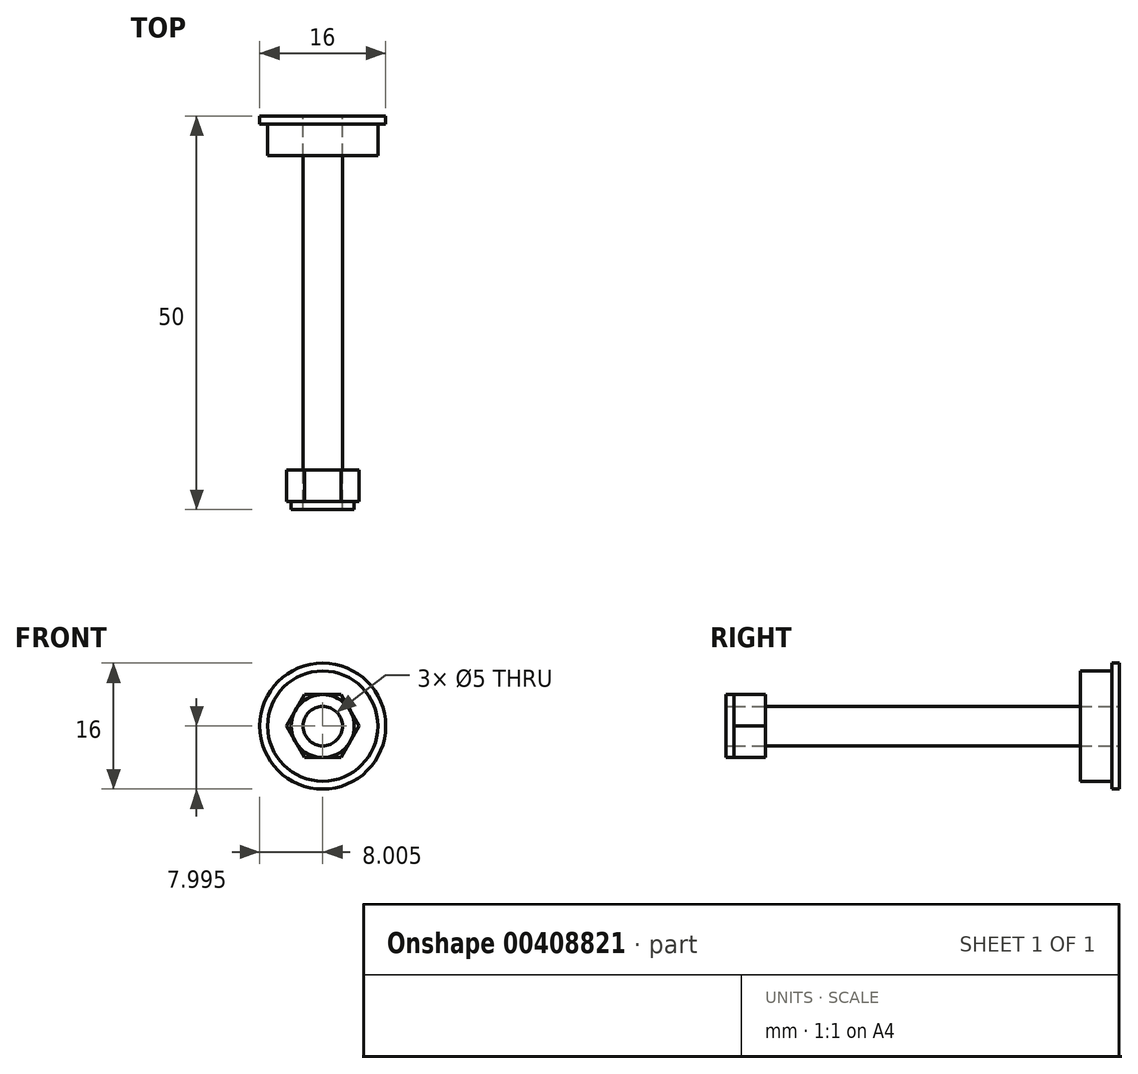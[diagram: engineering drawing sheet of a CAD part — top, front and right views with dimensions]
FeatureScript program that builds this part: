
annotation { "Feature Type Name" : "Feature", "Feature Type Description" : "" }
export const myFeature = defineFeature(function(context is Context, id is Id, definition is map)
    precondition{}
    {
        {
            var Q0;
            Q0=qCreatedBy(makeId("Front.planeOp"),FACE);
            var sketch = newSketch(context, id + "F0", { "sketchPlane" : qUnion([Q0])});
            skPoint(sketch, "E0", {"position": v(-33.67, 17.6) * mm});
            skLineSegment(sketch, "E1", {"start": v(-52.82, 17.6) * mm, "end": v(-12.98, 17.6) * mm, "construction": true});
            skLineSegment(sketch, "E2", {"start": v(-33.67, 39.41) * mm, "end": v(-33.67, -6.44) * mm, "construction": true});
            skCircle(sketch, "E3", {"center": v(-33.67, 17.6) * mm, "radius": 2.5 * mm});
            skCircle(sketch, "E4", {"center": v(-33.67, 17.6) * mm, "radius": 8 * mm});
            skSolve(sketch);
        }
        {
            var Q0;
            Q0=makeQuery(id+"F0.imprint","IMPRINT",FACE,{"disambiguationData":[TD([[makeQuery(id+"F0.imprint","IMPRINT",EDGE,{"derivedFrom":sQuery(id+"F0.wireOp",EDGE,"E3")}),-1.0]])]});
            extrude(context, id + "F1", {"entities" : qUnion([Q0]), "depth" : 1 * mm});
        }
        {
            var Q0;
            Q0=makeQuery(id+"F1.opExtrude","CAP_FACE",FACE,{"disambiguationData":[OSD([sQuery(id+"F0.wireOp",EDGE,"E3"),sQuery(id+"F0.wireOp",EDGE,"E4")])],"isStart":false});
            var sketch = newSketch(context, id + "F2", { "sketchPlane" : qUnion([Q0])});
            skCircle(sketch, "E5.0", {"center": v(-33.67, 17.6) * mm, "radius": 2.5 * mm});
            skCircle(sketch, "E6", {"center": v(-33.67, 17.6) * mm, "radius": 7 * mm});
            skSolve(sketch);
        }
        {
            var Q0;
            Q0=makeQuery(id+"F2.imprint","IMPRINT",FACE,{"disambiguationData":[TD([[makeQuery(id+"F2.imprint","IMPRINT",EDGE,{"derivedFrom":sQuery(id+"F2.wireOp",EDGE,"E5.0")}),-1.0]])]});
            extrude(context, id + "F3", {"entities" : qUnion([Q0]), "operationType" : NewBodyOperationType.ADD, "depth" : 4 * mm});
        }
        {
            var Q0;
            Q0=makeQuery(id+"F3.opExtrude","CAP_FACE",FACE,{"disambiguationData":[OSD([sQuery(id+"F2.wireOp",EDGE,"E5.0"),sQuery(id+"F2.wireOp",EDGE,"E6")])],"isStart":false});
            var sketch = newSketch(context, id + "F4", { "sketchPlane" : qUnion([Q0])});
            skCircle(sketch, "E7.0", {"center": v(-33.67, 17.6) * mm, "radius": 2.5 * mm});
            skSolve(sketch);
        }
        {
            var Q0;
            Q0=makeQuery(id+"F4.imprint","IMPRINT",FACE,{"disambiguationData":[TD([[makeQuery(id+"F4.imprint","IMPRINT",EDGE,{"derivedFrom":sQuery(id+"F4.wireOp",EDGE,"E7.0")}),1.0]])]});
            extrude(context, id + "F5", {"entities" : qUnion([Q0]), "depth" : 40 * mm});
        }
        {
            var Q0;
            Q0=makeQuery(id+"F5.opExtrude","CAP_FACE",FACE,{"disambiguationData":[OSD([sQuery(id+"F4.wireOp",EDGE,"E7.0")])],"isStart":false});
            var sketch = newSketch(context, id + "F6", { "sketchPlane" : qUnion([Q0])});
            skCircle(sketch, "E8.0", {"center": v(-33.67, 17.6) * mm, "radius": 2.5 * mm});
            skCircle(sketch, "E9.cCircle", {"center": v(-33.67, 17.6) * mm, "radius": 4 * mm, "construction": true});
            skLineSegment(sketch, "E9.0", {"start": v(-29.05, 17.6) * mm, "end": v(-31.36, 13.6) * mm});
            skLineSegment(sketch, "E9.1", {"start": v(-31.36, 13.6) * mm, "end": v(-35.97, 13.6) * mm});
            skLineSegment(sketch, "E9.2", {"start": v(-35.97, 13.6) * mm, "end": v(-38.28, 17.6) * mm});
            skLineSegment(sketch, "E9.3", {"start": v(-38.28, 17.6) * mm, "end": v(-35.97, 21.6) * mm});
            skLineSegment(sketch, "E9.4", {"start": v(-35.97, 21.6) * mm, "end": v(-31.36, 21.6) * mm});
            skLineSegment(sketch, "E9.5", {"start": v(-31.36, 21.6) * mm, "end": v(-29.05, 17.6) * mm});
            skPoint(sketch, "E9.0.midPoint", {"position": v(-30.2, 15.6) * mm});
            skSolve(sketch);
        }
        {
            var Q0;
            Q0=makeQuery(id+"F6.imprint","IMPRINT",FACE,{"disambiguationData":[TD([[makeQuery(id+"F6.imprint","IMPRINT",EDGE,{"derivedFrom":sQuery(id+"F6.wireOp",EDGE,"E8.0")}),-1.0]])]});
            extrude(context, id + "F7", {"entities" : qUnion([Q0]), "depth" : 4 * mm});
        }
        {
            var Q0;
            Q0=makeQuery(id+"F7.opExtrude","CAP_FACE",FACE,{"disambiguationData":[OSD([sQuery(id+"F6.wireOp",EDGE,"E8.0"),sQuery(id+"F6.wireOp",EDGE,"E9.0"),sQuery(id+"F6.wireOp",EDGE,"E9.1"),sQuery(id+"F6.wireOp",EDGE,"E9.2"),sQuery(id+"F6.wireOp",EDGE,"E9.3"),sQuery(id+"F6.wireOp",EDGE,"E9.4"),sQuery(id+"F6.wireOp",EDGE,"E9.5")])],"isStart":false});
            var sketch = newSketch(context, id + "F8", { "sketchPlane" : qUnion([Q0])});
            skCircle(sketch, "E10.0", {"center": v(-33.67, 17.6) * mm, "radius": 2.5 * mm});
            skCircle(sketch, "E11", {"center": v(-33.67, 17.6) * mm, "radius": 4 * mm});
            skSolve(sketch);
        }
        {
            var Q0;
            Q0=makeQuery(id+"F8.imprint","IMPRINT",FACE,{"disambiguationData":[TD([[makeQuery(id+"F8.imprint","IMPRINT",EDGE,{"derivedFrom":sQuery(id+"F8.wireOp",EDGE,"E10.0")}),-1.0]])]});
            extrude(context, id + "F9", {"entities" : qUnion([Q0]), "depth" : 1 * mm});
        }
    });
